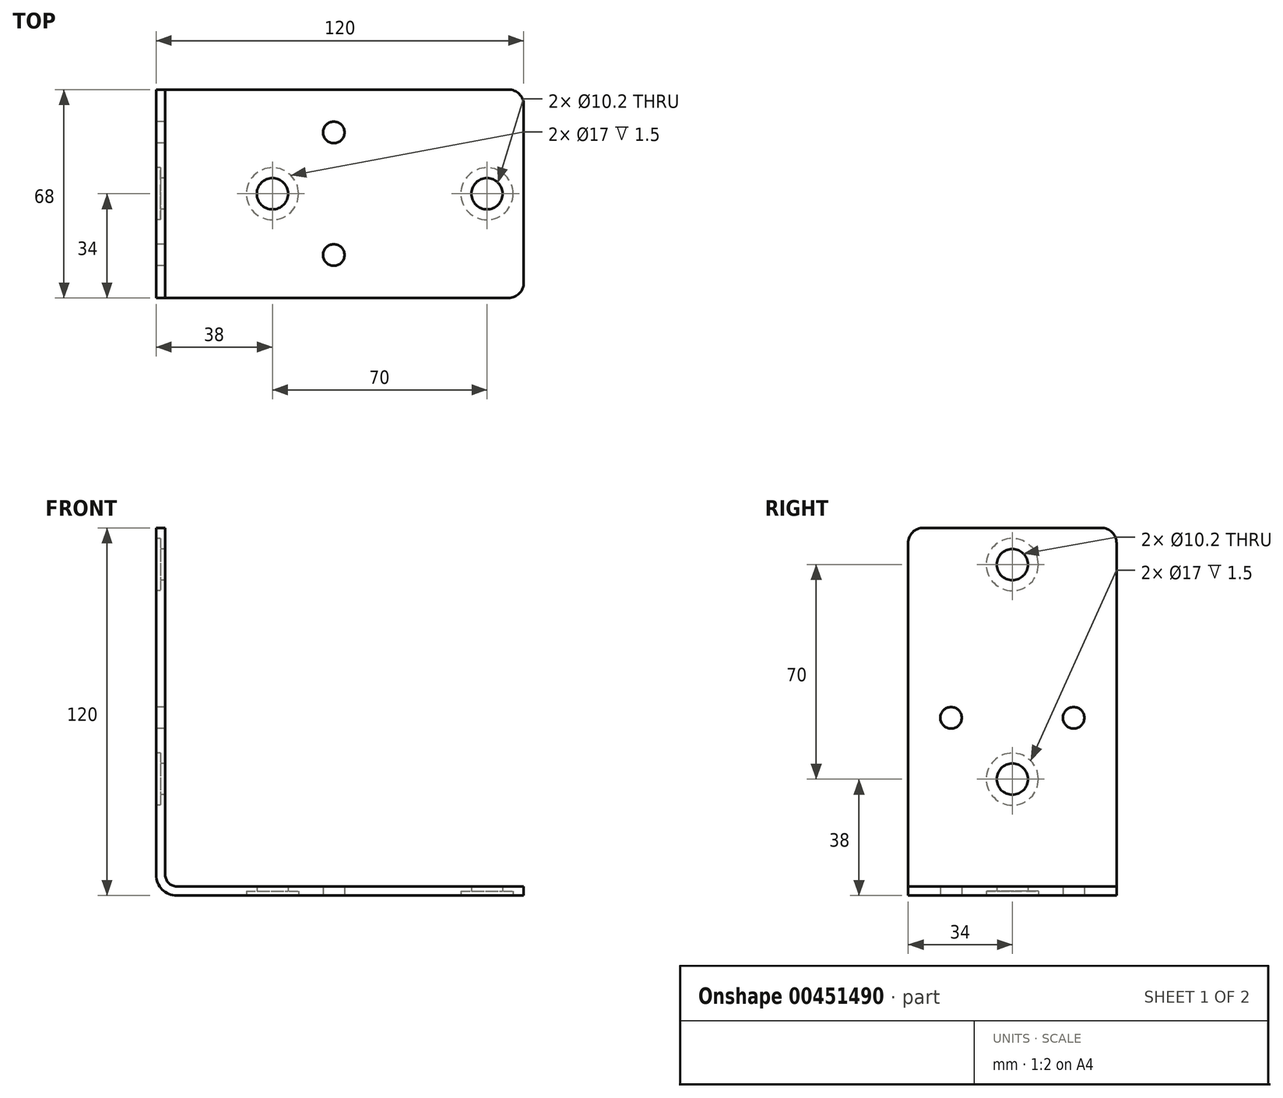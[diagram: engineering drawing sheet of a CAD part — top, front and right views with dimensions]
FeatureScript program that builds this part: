
annotation { "Feature Type Name" : "Feature", "Feature Type Description" : "" }
export const myFeature = defineFeature(function(context is Context, id is Id, definition is map)
    precondition{}
    {
        {
            var Q0;
            Q0=qCreatedBy(makeId("Front.planeOp"),FACE);
            var sketch = newSketch(context, id + "F0", { "sketchPlane" : qUnion([Q0])});
            skLineSegment(sketch, "E0", {"start": v(0, 120) * mm, "end": v(0, 0) * mm});
            skLineSegment(sketch, "E1", {"start": v(0, 0) * mm, "end": v(120, 0) * mm});
            skLineSegment(sketch, "E2.0", {"start": v(3, 3) * mm, "end": v(120, 3) * mm});
            skLineSegment(sketch, "E2.1", {"start": v(3, 120) * mm, "end": v(3, 3) * mm});
            skLineSegment(sketch, "E3", {"start": v(0, 120) * mm, "end": v(3, 120) * mm});
            skLineSegment(sketch, "E4", {"start": v(120, 0) * mm, "end": v(120, 3) * mm});
            skSolve(sketch);
        }
        {
            var Q0;
            Q0=qSketchRegion(id+"F0",true);
            extrude(context, id + "F1", {"entities" : qUnion([Q0]), "oppositeDirection" : true, "depth" : 68 * mm});
        }
        {
            var Q0;
            Q0=makeQuery(id+"F1.opExtrude","SWEPT_EDGE",EDGE,{"disambiguationData":[OSD([sQuery(id+"F0.wireOp",EDGE,"E2.0"),sQuery(id+"F0.wireOp",EDGE,"E2.1")])]});
            fillet(context, id + "F2", {"entities" : qUnion([Q0]), "radius" : 3.8 * mm, "tangentPropagation" : true, "allowEdgeOverflow" : false});
        }
        {
            var Q0;
            Q0=makeQuery(id+"F1.opExtrude","SWEPT_EDGE",EDGE,{"disambiguationData":[OSD([sQuery(id+"F0.wireOp",EDGE,"E0"),sQuery(id+"F0.wireOp",EDGE,"E1")])]});
            fillet(context, id + "F3", {"entities" : qUnion([Q0]), "radius" : 6.8 * mm, "tangentPropagation" : true, "allowEdgeOverflow" : false});
        }
        {
            var Q0;
            Q0=makeQuery(id+"F1.opExtrude","CAP_EDGE",EDGE,{"disambiguationData":[OSD([sQuery(id+"F0.wireOp",EDGE,"E3")])],"isStart":true});
            var Q1;
            Q1=makeQuery(id+"F1.opExtrude","CAP_EDGE",EDGE,{"disambiguationData":[OSD([sQuery(id+"F0.wireOp",EDGE,"E4")])],"isStart":true});
            var Q2;
            Q2=makeQuery(id+"F1.opExtrude","CAP_EDGE",EDGE,{"disambiguationData":[OSD([sQuery(id+"F0.wireOp",EDGE,"E4")])],"isStart":false});
            var Q3;
            Q3=makeQuery(id+"F1.opExtrude","CAP_EDGE",EDGE,{"disambiguationData":[OSD([sQuery(id+"F0.wireOp",EDGE,"E3")])],"isStart":false});
            fillet(context, id + "F4", {"entities" : qUnion([Q0, Q1, Q2, Q3]), "radius" : 5 * mm, "tangentPropagation" : true, "allowEdgeOverflow" : false});
        }
        {
            var Q0;
            Q0=makeQuery(id+"F1.opExtrude","SWEPT_FACE",FACE,{"disambiguationData":[OSD([sQuery(id+"F0.wireOp",EDGE,"E1")])]});
            var sketch = newSketch(context, id + "F5", { "sketchPlane" : qUnion([Q0])});
            skCircle(sketch, "E5", {"center": v(108, -34) * mm, "radius": 5.1 * mm});
            skPoint(sketch, "E5.centerSnap0", {"position": v(120, -34) * mm});
            skCircle(sketch, "E6", {"center": v(38, -34) * mm, "radius": 5.1 * mm});
            skCircle(sketch, "E7", {"center": v(58, -14) * mm, "radius": 3.5 * mm});
            skCircle(sketch, "E8", {"center": v(58, -54) * mm, "radius": 3.5 * mm});
            skSolve(sketch);
        }
        {
            var Q0;
            Q0=qSketchRegion(id+"F5",true);
            extrude(context, id + "F6", {"entities" : qUnion([Q0]), "operationType" : NewBodyOperationType.REMOVE, "endBound" : BoundingType.THROUGH_ALL, "oppositeDirection" : true, "depth" : 25 * mm});
        }
        {
            var Q0;
            Q0=makeQuery(id+"F1.opExtrude","SWEPT_FACE",FACE,{"disambiguationData":[OSD([sQuery(id+"F0.wireOp",EDGE,"E0")])]});
            var sketch = newSketch(context, id + "F7", { "sketchPlane" : qUnion([Q0])});
            skCircle(sketch, "E9", {"center": v(-34, 108) * mm, "radius": 5.1 * mm});
            skPoint(sketch, "E9.centerSnap0", {"position": v(-34, 120) * mm});
            skCircle(sketch, "E10", {"center": v(-34, 38) * mm, "radius": 5.1 * mm});
            skCircle(sketch, "E11", {"center": v(-14, 58) * mm, "radius": 3.5 * mm});
            skCircle(sketch, "E12", {"center": v(-54, 58) * mm, "radius": 3.5 * mm});
            skSolve(sketch);
        }
        {
            var Q0;
            Q0=qSketchRegion(id+"F7",true);
            extrude(context, id + "F8", {"entities" : qUnion([Q0]), "operationType" : NewBodyOperationType.REMOVE, "endBound" : BoundingType.THROUGH_ALL, "oppositeDirection" : true, "depth" : 25 * mm});
        }
        {
            var Q0;
            Q0=makeQuery(id+"F1.opExtrude","SWEPT_FACE",FACE,{"disambiguationData":[OSD([sQuery(id+"F0.wireOp",EDGE,"E0")])]});
            var sketch = newSketch(context, id + "F9", { "sketchPlane" : qUnion([Q0])});
            skCircle(sketch, "E13", {"center": v(-34, 108) * mm, "radius": 8.5 * mm});
            skCircle(sketch, "E14", {"center": v(-34, 38) * mm, "radius": 8.5 * mm});
            skSolve(sketch);
        }
        {
            var Q0;
            Q0=qSketchRegion(id+"F9",true);
            extrude(context, id + "F10", {"entities" : qUnion([Q0]), "operationType" : NewBodyOperationType.REMOVE, "oppositeDirection" : true, "depth" : 1.5 * mm});
        }
        {
            var Q0;
            Q0=makeQuery(id+"F1.opExtrude","SWEPT_FACE",FACE,{"disambiguationData":[OSD([sQuery(id+"F0.wireOp",EDGE,"E1")])]});
            var sketch = newSketch(context, id + "F11", { "sketchPlane" : qUnion([Q0])});
            skCircle(sketch, "E15", {"center": v(38, -34) * mm, "radius": 8.5 * mm});
            skCircle(sketch, "E16", {"center": v(108, -34) * mm, "radius": 8.5 * mm});
            skSolve(sketch);
        }
        {
            var Q0;
            Q0=qSketchRegion(id+"F11",true);
            extrude(context, id + "F12", {"entities" : qUnion([Q0]), "operationType" : NewBodyOperationType.REMOVE, "oppositeDirection" : true, "depth" : 1.5 * mm});
        }
    });
